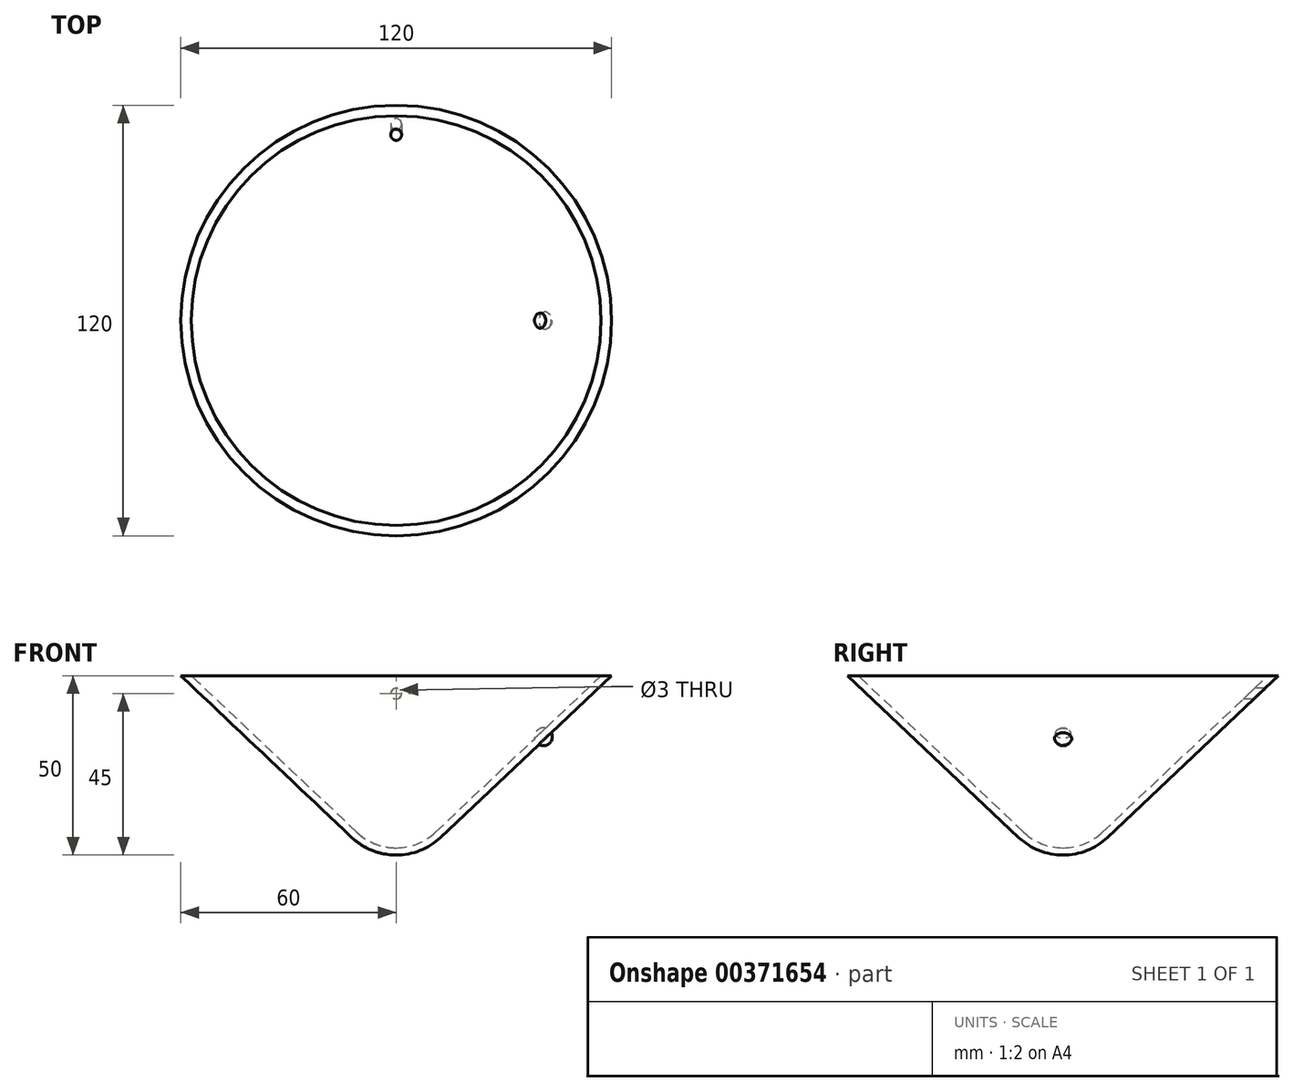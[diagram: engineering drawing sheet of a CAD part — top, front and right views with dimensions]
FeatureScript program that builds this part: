
annotation { "Feature Type Name" : "Feature", "Feature Type Description" : "" }
export const myFeature = defineFeature(function(context is Context, id is Id, definition is map)
    precondition{}
    {
        {
            var Q0;
            Q0=qCreatedBy(makeId("Front.planeOp"),FACE);
            var sketch = newSketch(context, id + "F0", { "sketchPlane" : qUnion([Q0])});
            skLineSegment(sketch, "E0", {"start": v(0, 0) * mm, "end": v(-60, 0) * mm});
            skLineSegment(sketch, "E1", {"start": v(-60, 0) * mm, "end": v(-12.37, -45.07) * mm});
            skLineSegment(sketch, "E2", {"start": v(0, -50) * mm, "end": v(0, 0) * mm});
            skArc(sketch, "E3", {"start": v(-12.37, -45.07) * mm, "mid": v(-6.66, -48.72) * mm, "end": v(0, -50) * mm});
            skPoint(sketch, "E4.orphan", {"position": v(0, -56.78) * mm});
            skLineSegment(sketch, "E5", {"start": v(0, 27.19) * mm, "end": v(0, -74.54) * mm, "construction": true});
            skSolve(sketch);
        }
        {
            var Q0;
            Q0=makeQuery(id+"F0.imprint","IMPRINT",FACE,{"disambiguationData":[TD([[makeQuery(id+"F0.imprint","IMPRINT",EDGE,{"derivedFrom":sQuery(id+"F0.wireOp",EDGE,"E0")}),1.0]])]});
            var Q1;
            Q1=sQuery(id+"F0.wireOp",EDGE,"E2");
            revolve(context, id + "F1", {"entities" : qUnion([Q0]), "axis" : qUnion([Q1]), "revolveType" : RevolveType.FULL});
        }
        {
            var Q0;
            Q0=makeQuery(id+"F1.opRevolve","SWEPT_FACE",FACE,{"disambiguationData":[OSD([sQuery(id+"F0.wireOp",EDGE,"E0")])]});
            shell(context, id + "F2", {"entities" : qUnion([Q0]), "thickness" : 2 * mm});
        }
        {
            var Q0;
            Q0=qCreatedBy(makeId("Front.planeOp"),FACE);
            var sketch = newSketch(context, id + "F3", { "sketchPlane" : qUnion([Q0])});
            skCircle(sketch, "E6", {"center": v(0, -5) * mm, "radius": 1.5 * mm});
            skSolve(sketch);
        }
        {
            var Q0;
            Q0 = qSketchRegion(id + "F3", true);
            extrude(context, id + "F4", {"entities" : qUnion([Q0]), "operationType" : NewBodyOperationType.REMOVE, "endBound" : BoundingType.THROUGH_ALL, "oppositeDirection" : true, "depth" : 25 * mm});
        }
        {
            var Q0;
            Q0=qCreatedBy(makeId("Front.planeOp"),FACE);
            var sketch = newSketch(context, id + "F5", { "sketchPlane" : qUnion([Q0])});
            skArc(sketch, "E7", {"start": v(39.3, -18.83) * mm, "mid": v(42.82, -18.72) * mm, "end": v(42.73, -15.2) * mm});
            skLineSegment(sketch, "E8", {"start": v(39.3, -18.83) * mm, "end": v(42.73, -15.2) * mm});
            skSolve(sketch);
        }
        {
            var Q0;
            Q0 = qSketchRegion(id + "F5", true);
            var Q1;
            Q1=sQuery(id+"F5.wireOp",EDGE,"E8");
            revolve(context, id + "F6", {"operationType" : NewBodyOperationType.ADD, "entities" : qUnion([Q0]), "axis" : qUnion([Q1]), "revolveType" : RevolveType.FULL});
        }
    });
